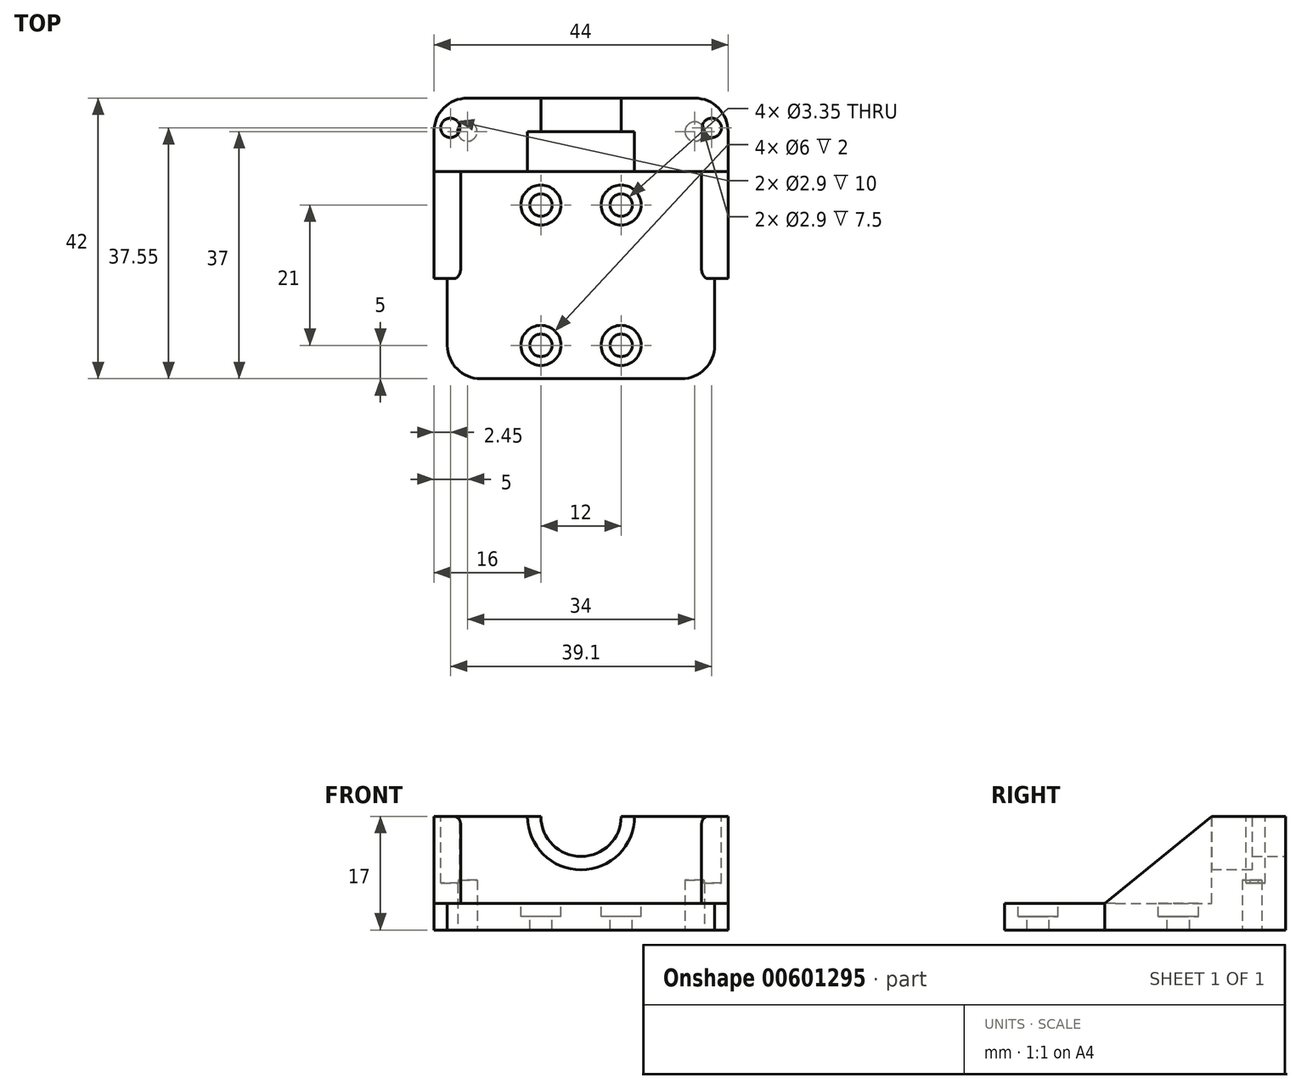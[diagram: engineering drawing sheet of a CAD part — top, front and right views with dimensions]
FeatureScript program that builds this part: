
annotation { "Feature Type Name" : "Feature", "Feature Type Description" : "" }
export const myFeature = defineFeature(function(context is Context, id is Id, definition is map)
    precondition{}
    {
        {
            var Q0;
            Q0=qCreatedBy(makeId("Top.planeOp"),FACE);
            var sketch = newSketch(context, id + "F0", { "sketchPlane" : qUnion([Q0])});
            skLineSegment(sketch, "E0.bottom", {"start": v(0, 0) * mm, "end": v(40, 0) * mm});
            skLineSegment(sketch, "E0.top", {"start": v(0, 42) * mm, "end": v(40, 42) * mm});
            skLineSegment(sketch, "E0.left", {"start": v(0, 0) * mm, "end": v(0, 42) * mm});
            skLineSegment(sketch, "E0.right", {"start": v(40, 0) * mm, "end": v(40, 42) * mm});
            skSolve(sketch);
        }
        {
            var Q0;
            Q0=qSketchRegion(id+"F0",true);
            extrude(context, id + "F1", {"entities" : qUnion([Q0]), "depth" : 4 * mm});
        }
        {
            var Q0;
            Q0=makeQuery(id+"F1.opExtrude","CAP_FACE",FACE,{"disambiguationData":[OSD([sQuery(id+"F0.wireOp",EDGE,"E0.bottom"),sQuery(id+"F0.wireOp",EDGE,"E0.top"),sQuery(id+"F0.wireOp",EDGE,"E0.left"),sQuery(id+"F0.wireOp",EDGE,"E0.right")])],"isStart":false});
            var sketch = newSketch(context, id + "F2", { "sketchPlane" : qUnion([Q0])});
            skCircle(sketch, "E1", {"center": v(14, 26) * mm, "radius": 1.68 * mm});
            skCircle(sketch, "E2", {"center": v(26, 26) * mm, "radius": 1.68 * mm});
            skCircle(sketch, "E3", {"center": v(14, 5) * mm, "radius": 1.68 * mm});
            skCircle(sketch, "E4", {"center": v(26, 5) * mm, "radius": 1.68 * mm});
            skLineSegment(sketch, "E5", {"start": v(14, 26) * mm, "end": v(0, 26) * mm});
            skLineSegment(sketch, "E6", {"start": v(26, 5) * mm, "end": v(40, 5) * mm});
            skCircle(sketch, "E7", {"center": v(14, 26) * mm, "radius": 3 * mm});
            skCircle(sketch, "E8", {"center": v(26, 26) * mm, "radius": 3 * mm});
            skCircle(sketch, "E9", {"center": v(14, 5) * mm, "radius": 3 * mm});
            skCircle(sketch, "E10", {"center": v(26, 5) * mm, "radius": 3 * mm});
            skSolve(sketch);
        }
        {
            var Q0;
            Q0=makeQuery(id+"F2.imprint","IMPRINT",FACE,{"disambiguationData":[TD([[makeQuery(id+"F2.imprint","IMPRINT",EDGE,{"derivedFrom":sQuery(id+"F2.wireOp",EDGE,"E1")}),1.0]])]});
            var Q1;
            Q1=makeQuery(id+"F2.imprint","IMPRINT",FACE,{"disambiguationData":[TD([[makeQuery(id+"F2.imprint","IMPRINT",EDGE,{"derivedFrom":sQuery(id+"F2.wireOp",EDGE,"E2")}),1.0]])]});
            var Q2;
            Q2=makeQuery(id+"F2.imprint","IMPRINT",FACE,{"disambiguationData":[TD([[makeQuery(id+"F2.imprint","IMPRINT",EDGE,{"derivedFrom":sQuery(id+"F2.wireOp",EDGE,"E4")}),1.0]])]});
            var Q3;
            Q3=makeQuery(id+"F2.imprint","IMPRINT",FACE,{"disambiguationData":[TD([[makeQuery(id+"F2.imprint","IMPRINT",EDGE,{"derivedFrom":sQuery(id+"F2.wireOp",EDGE,"E3")}),1.0]])]});
            extrude(context, id + "F3", {"entities" : qUnion([Q0, Q1, Q2, Q3]), "operationType" : NewBodyOperationType.REMOVE, "oppositeDirection" : true, "depth" : 25 * mm});
        }
        {
            var Q0;
            Q0=makeQuery(id+"F1.opExtrude","CAP_FACE",FACE,{"disambiguationData":[OSD([sQuery(id+"F0.wireOp",EDGE,"E0.bottom"),sQuery(id+"F0.wireOp",EDGE,"E0.top"),sQuery(id+"F0.wireOp",EDGE,"E0.left"),sQuery(id+"F0.wireOp",EDGE,"E0.right")])],"isStart":false});
            var sketch = newSketch(context, id + "F4", { "sketchPlane" : qUnion([Q0])});
            skLineSegment(sketch, "E11.bottom", {"start": v(0, 42) * mm, "end": v(40, 42) * mm});
            skLineSegment(sketch, "E11.top", {"start": v(0, 31) * mm, "end": v(40, 31) * mm});
            skLineSegment(sketch, "E11.left", {"start": v(0, 42) * mm, "end": v(0, 31) * mm});
            skLineSegment(sketch, "E11.right", {"start": v(40, 42) * mm, "end": v(40, 31) * mm});
            skSolve(sketch);
        }
        {
            var Q0;
            Q0=qSketchRegion(id+"F4",true);
            extrude(context, id + "F5", {"entities" : qUnion([Q0]), "operationType" : NewBodyOperationType.ADD, "depth" : 13 * mm, "offsetDistance" : 25 * mm});
        }
        {
            var Q0;
            Q0=makeQuery(id+"F5.boolean.opBoolean","MERGE",FACE,{"derivedFrom":[makeQuery(id+"F1.opExtrude","SWEPT_FACE",FACE,{"disambiguationData":[OSD([sQuery(id+"F0.wireOp",EDGE,"E0.top")])]}),makeQuery(id+"F5.opExtrude","SWEPT_FACE",FACE,{"disambiguationData":[OSD([sQuery(id+"F4.wireOp",EDGE,"E11.bottom")])]})]});
            var sketch = newSketch(context, id + "F6", { "sketchPlane" : qUnion([Q0])});
            skCircle(sketch, "E12", {"center": v(-20, 17) * mm, "radius": 6 * mm});
            skSolve(sketch);
        }
        {
            var Q0;
            {var subQ0=makeQuery(id+"F5.opExtrude","CAP_EDGE",EDGE,{"disambiguationData":[OSD([sQuery(id+"F4.wireOp",EDGE,"E11.bottom")])],"isStart":false});var subQ1=sQuery(id+"F6.wireOp",EDGE,"E12");var subQ3=makeQuery(id+"F6.imprint","INTERSECT",VERTEX,{"disambiguationData":[OD(0.0)],"derivedFrom":[subQ0,subQ1]});Q0=makeQuery(id+"F6.imprint","IMPRINT",FACE,{"disambiguationData":[TD([[makeQuery(id+"F6.imprint","IMPRINT",EDGE,{"disambiguationData":[TD([[subQ3,1.0]])],"derivedFrom":subQ1}),1.0]])]});}
            extrude(context, id + "F7", {"entities" : qUnion([Q0]), "operationType" : NewBodyOperationType.REMOVE, "oppositeDirection" : true, "depth" : 6 * mm});
        }
        {
            var Q0;
            Q0=makeQuery(id+"F5.opExtrude","SWEPT_FACE",FACE,{"disambiguationData":[OSD([sQuery(id+"F4.wireOp",EDGE,"E11.top")])]});
            var sketch = newSketch(context, id + "F8", { "sketchPlane" : qUnion([Q0])});
            skCircle(sketch, "E13", {"center": v(20, 17) * mm, "radius": 8 * mm});
            skSolve(sketch);
        }
        {
            var Q0;
            Q0=qSketchRegion(id+"F8",true);
            extrude(context, id + "F9", {"entities" : qUnion([Q0]), "operationType" : NewBodyOperationType.REMOVE, "oppositeDirection" : true, "depth" : 6 * mm});
        }
        {
            var Q0;
            Q0=makeQuery(id+"F2.imprint","IMPRINT",FACE,{"disambiguationData":[TD([[makeQuery(id+"F2.imprint","IMPRINT",EDGE,{"derivedFrom":sQuery(id+"F2.wireOp",EDGE,"E1")}),-1.0]])]});
            var Q1;
            Q1=makeQuery(id+"F2.imprint","IMPRINT",FACE,{"disambiguationData":[TD([[makeQuery(id+"F2.imprint","IMPRINT",EDGE,{"derivedFrom":sQuery(id+"F2.wireOp",EDGE,"E2")}),-1.0]])]});
            var Q2;
            Q2=makeQuery(id+"F2.imprint","IMPRINT",FACE,{"disambiguationData":[TD([[makeQuery(id+"F2.imprint","IMPRINT",EDGE,{"derivedFrom":sQuery(id+"F2.wireOp",EDGE,"E4")}),-1.0]])]});
            var Q3;
            Q3=makeQuery(id+"F2.imprint","IMPRINT",FACE,{"disambiguationData":[TD([[makeQuery(id+"F2.imprint","IMPRINT",EDGE,{"derivedFrom":sQuery(id+"F2.wireOp",EDGE,"E3")}),-1.0]])]});
            extrude(context, id + "F10", {"entities" : qUnion([Q0, Q1, Q2, Q3]), "operationType" : NewBodyOperationType.REMOVE, "oppositeDirection" : true, "depth" : 2 * mm});
        }
        {
            var Q0;
            Q0=makeQuery(id+"F5.boolean.opBoolean","MERGE",FACE,{"derivedFrom":[makeQuery(id+"F1.opExtrude","SWEPT_FACE",FACE,{"disambiguationData":[OSD([sQuery(id+"F0.wireOp",EDGE,"E0.left")])]}),makeQuery(id+"F5.opExtrude","SWEPT_FACE",FACE,{"disambiguationData":[OSD([sQuery(id+"F4.wireOp",EDGE,"E11.left")])]})]});
            var sketch = newSketch(context, id + "F11", { "sketchPlane" : qUnion([Q0])});
            skLineSegment(sketch, "E14.bottom", {"start": v(-42, 0) * mm, "end": v(-31, 0) * mm});
            skLineSegment(sketch, "E14.top", {"start": v(-42, 17) * mm, "end": v(-31, 17) * mm});
            skLineSegment(sketch, "E14.left", {"start": v(-42, 0) * mm, "end": v(-42, 17) * mm});
            skLineSegment(sketch, "E14.right", {"start": v(-31, 0) * mm, "end": v(-31, 17) * mm});
            skSolve(sketch);
        }
        {
            var Q0;
            Q0=qSketchRegion(id+"F11",true);
            extrude(context, id + "F12", {"entities" : qUnion([Q0]), "operationType" : NewBodyOperationType.ADD, "depth" : 2 * mm});
        }
        {
            var Q0;
            Q0=makeQuery(id+"F1.opExtrude","SWEPT_EDGE",EDGE,{"disambiguationData":[OSD([sQuery(id+"F0.wireOp",EDGE,"E0.bottom"),sQuery(id+"F0.wireOp",EDGE,"E0.left")])]});
            var Q1;
            Q1=makeQuery(id+"F1.opExtrude","SWEPT_EDGE",EDGE,{"disambiguationData":[OSD([sQuery(id+"F0.wireOp",EDGE,"E0.bottom"),sQuery(id+"F0.wireOp",EDGE,"E0.right")])]});
            var Q2;
            Q2=makeQuery(id+"F17.opExtrude","TWEAK_EDGE",EDGE,{"derivedFrom":[makeQuery(id+"F1.opExtrude","SWEPT_EDGE",EDGE,{"disambiguationData":[OSD([sQuery(id+"F0.wireOp",EDGE,"E0.bottom"),sQuery(id+"F0.wireOp",EDGE,"E0.left")])]}),makeQuery(id+"F12.opExtrude","CAP_FACE",FACE,{"disambiguationData":[OSD([sQuery(id+"F11.wireOp",EDGE,"E14.bottom"),sQuery(id+"F11.wireOp",EDGE,"E14.top"),sQuery(id+"F11.wireOp",EDGE,"E14.left"),sQuery(id+"F11.wireOp",EDGE,"E14.right")])],"isStart":false})]});
            fillet(context, id + "F13", {"entities" : qUnion([Q0, Q1, Q2]), "radius" : 5 * mm, "tangentPropagation" : true, "allowEdgeOverflow" : false});
        }
        {
            var Q0;
            Q0=makeQuery(id+"F5.boolean.opBoolean","MERGE",FACE,{"derivedFrom":[makeQuery(id+"F1.opExtrude","SWEPT_FACE",FACE,{"disambiguationData":[OSD([sQuery(id+"F0.wireOp",EDGE,"E0.right")])]}),makeQuery(id+"F5.opExtrude","SWEPT_FACE",FACE,{"disambiguationData":[OSD([sQuery(id+"F4.wireOp",EDGE,"E11.right")])]})]});
            var sketch = newSketch(context, id + "F14", { "sketchPlane" : qUnion([Q0])});
            skLineSegment(sketch, "E15.bottom", {"start": v(42, 0) * mm, "end": v(31, 0) * mm});
            skLineSegment(sketch, "E15.top", {"start": v(42, 17) * mm, "end": v(31, 17) * mm});
            skLineSegment(sketch, "E15.left", {"start": v(42, 0) * mm, "end": v(42, 17) * mm});
            skLineSegment(sketch, "E15.right", {"start": v(31, 0) * mm, "end": v(31, 17) * mm});
            skSolve(sketch);
        }
        {
            var Q0;
            Q0=qSketchRegion(id+"F14",true);
            extrude(context, id + "F15", {"entities" : qUnion([Q0]), "operationType" : NewBodyOperationType.ADD, "depth" : 2 * mm});
        }
        {
            var Q0;
            Q0=qSketchRegion(id+"F14",true);
            extrude(context, id + "F16", {"entities" : qUnion([Q0]), "operationType" : NewBodyOperationType.ADD, "depth" : 2 * mm});
        }
        {
            var Q0;
            Q0=makeQuery(id+"F5.boolean.opBoolean","MERGE",FACE,{"derivedFrom":[makeQuery(id+"F1.opExtrude","SWEPT_FACE",FACE,{"disambiguationData":[OSD([sQuery(id+"F0.wireOp",EDGE,"E0.left")])]}),makeQuery(id+"F5.opExtrude","SWEPT_FACE",FACE,{"disambiguationData":[OSD([sQuery(id+"F4.wireOp",EDGE,"E11.left")])]})]});
            var Q1;
            Q1=makeQuery(id+"F12.opExtrude","CAP_FACE",FACE,{"disambiguationData":[OSD([sQuery(id+"F11.wireOp",EDGE,"E14.bottom"),sQuery(id+"F11.wireOp",EDGE,"E14.top"),sQuery(id+"F11.wireOp",EDGE,"E14.left"),sQuery(id+"F11.wireOp",EDGE,"E14.right")])],"isStart":false});
            extrude(context, id + "F17", {"entities" : qUnion([Q0]), "operationType" : NewBodyOperationType.ADD, "endBound" : BoundingType.UP_TO_SURFACE, "depth" : 25 * mm, "endBoundEntityFace" : qUnion([Q1]), "offsetDistance" : 25 * mm});
        }
        {
            var Q0;
            Q0=makeQuery(id+"F5.boolean.opBoolean","MERGE",FACE,{"derivedFrom":[makeQuery(id+"F1.opExtrude","SWEPT_FACE",FACE,{"disambiguationData":[OSD([sQuery(id+"F0.wireOp",EDGE,"E0.right")])]}),makeQuery(id+"F5.opExtrude","SWEPT_FACE",FACE,{"disambiguationData":[OSD([sQuery(id+"F4.wireOp",EDGE,"E11.right")])]})]});
            var Q1;
            Q1=makeQuery(id+"F15.opExtrude","CAP_FACE",FACE,{"disambiguationData":[OSD([sQuery(id+"F14.wireOp",EDGE,"E15.bottom"),sQuery(id+"F14.wireOp",EDGE,"E15.top"),sQuery(id+"F14.wireOp",EDGE,"E15.left"),sQuery(id+"F14.wireOp",EDGE,"E15.right")])],"isStart":false});
            extrude(context, id + "F18", {"entities" : qUnion([Q0]), "operationType" : NewBodyOperationType.ADD, "endBound" : BoundingType.UP_TO_SURFACE, "depth" : 25 * mm, "endBoundEntityFace" : qUnion([Q1]), "offsetDistance" : 25 * mm});
        }
        {
            var Q0;
            {var subQ0=sQuery(id+"F4.wireOp",EDGE,"E11.bottom");var subQ1=sQuery(id+"F4.wireOp",EDGE,"E11.top");var subQ2=sQuery(id+"F4.wireOp",EDGE,"E11.left");Q0=makeQuery(id+"F9.boolean.opBoolean","SPLIT",FACE,{"disambiguationData":[TD([makeQuery(id+"F1.opExtrude","SWEPT_FACE",FACE,{"disambiguationData":[OSD([sQuery(id+"F0.wireOp",EDGE,"E0.left")])]})])],"derivedFrom":makeQuery(id+"F5.opExtrude","CAP_FACE",FACE,{"disambiguationData":[OSD([subQ0,subQ1,subQ2,sQuery(id+"F4.wireOp",EDGE,"E11.right")])],"isStart":false})});}
            var sketch = newSketch(context, id + "F19", { "sketchPlane" : qUnion([Q0])});
            skCircle(sketch, "E16", {"center": v(0.45, 37.55) * mm, "radius": 1.45 * mm});
            skCircle(sketch, "E17", {"center": v(39.55, 37.55) * mm, "radius": 1.45 * mm});
            skSolve(sketch);
        }
        {
            var Q0;
            Q0=qSketchRegion(id+"F19",true);
            extrude(context, id + "F20", {"entities" : qUnion([Q0]), "operationType" : NewBodyOperationType.REMOVE, "oppositeDirection" : true, "depth" : 10 * mm, "offsetDistance" : 25 * mm});
        }
        {
            var Q0;
            Q0=makeQuery(id+"F12.opExtrude","CAP_EDGE",EDGE,{"disambiguationData":[OSD([sQuery(id+"F11.wireOp",EDGE,"E14.left")])],"isStart":false});
            var Q1;
            Q1=makeQuery(id+"F15.opExtrude","CAP_EDGE",EDGE,{"disambiguationData":[OSD([sQuery(id+"F14.wireOp",EDGE,"E15.left")])],"isStart":false});
            fillet(context, id + "F21", {"entities" : qUnion([Q0, Q1]), "radius" : 5 * mm, "tangentPropagation" : true, "allowEdgeOverflow" : false});
        }
        {
            var Q0;
            Q0=makeQuery(id+"F2.imprint","IMPRINT",FACE,{"disambiguationData":[TD([[makeQuery(id+"F2.imprint","IMPRINT",EDGE,{"derivedFrom":sQuery(id+"F2.wireOp",EDGE,"E1")}),-1.0]])]});
            var Q1;
            Q1=makeQuery(id+"F2.imprint","IMPRINT",FACE,{"disambiguationData":[TD([[makeQuery(id+"F2.imprint","IMPRINT",EDGE,{"derivedFrom":sQuery(id+"F2.wireOp",EDGE,"E2")}),-1.0]])]});
            var Q2;
            Q2=makeQuery(id+"F2.imprint","IMPRINT",FACE,{"disambiguationData":[TD([[makeQuery(id+"F2.imprint","IMPRINT",EDGE,{"derivedFrom":sQuery(id+"F2.wireOp",EDGE,"E1")}),1.0]])]});
            var Q3;
            Q3=makeQuery(id+"F2.imprint","IMPRINT",FACE,{"disambiguationData":[TD([[makeQuery(id+"F2.imprint","IMPRINT",EDGE,{"derivedFrom":sQuery(id+"F2.wireOp",EDGE,"E2")}),1.0]])]});
            extrude(context, id + "F22", {"entities" : qUnion([Q0, Q1, Q2, Q3]), "operationType" : NewBodyOperationType.REMOVE, "depth" : 25 * mm});
        }
        {
            var Q0;
            Q0=makeQuery(id+"F15.boolean.opBoolean","MERGE",FACE,{"derivedFrom":[makeQuery(id+"F12.boolean.opBoolean","MERGE",FACE,{"derivedFrom":[makeQuery(id+"F1.opExtrude","CAP_FACE",FACE,{"disambiguationData":[OSD([sQuery(id+"F0.wireOp",EDGE,"E0.bottom"),sQuery(id+"F0.wireOp",EDGE,"E0.top"),sQuery(id+"F0.wireOp",EDGE,"E0.left"),sQuery(id+"F0.wireOp",EDGE,"E0.right")])],"isStart":true}),makeQuery(id+"F12.opExtrude","SWEPT_FACE",FACE,{"disambiguationData":[OSD([sQuery(id+"F11.wireOp",EDGE,"E14.bottom")])]})]}),makeQuery(id+"F15.opExtrude","SWEPT_FACE",FACE,{"disambiguationData":[OSD([sQuery(id+"F14.wireOp",EDGE,"E15.bottom")])]})]});
            var sketch = newSketch(context, id + "F23", { "sketchPlane" : qUnion([Q0])});
            skCircle(sketch, "E18", {"center": v(37, -37) * mm, "radius": 1.45 * mm});
            skCircle(sketch, "E19", {"center": v(3, -37) * mm, "radius": 1.45 * mm});
            skSolve(sketch);
        }
        {
            var Q0;
            Q0 = qSketchRegion(id + "F23", true);
            extrude(context, id + "F24", {"entities" : qUnion([Q0]), "operationType" : NewBodyOperationType.REMOVE, "oppositeDirection" : true, "depth" : 7.5 * mm, "offsetDistance" : 25 * mm});
        }
        {
            var Q0;
            Q0=makeQuery(id+"F17.opExtrude","SWEPT_FACE",FACE,{"disambiguationData":[OSD([sQuery(id+"F0.wireOp",EDGE,"E0.bottom"),sQuery(id+"F0.wireOp",EDGE,"E0.left"),sQuery(id+"F4.wireOp",EDGE,"E11.left")])]});
            var Q1;
            Q1=makeQuery(id+"F18.opExtrude","SWEPT_FACE",FACE,{"disambiguationData":[OSD([sQuery(id+"F0.wireOp",EDGE,"E0.bottom"),sQuery(id+"F0.wireOp",EDGE,"E0.right"),sQuery(id+"F4.wireOp",EDGE,"E11.right")])]});
            extrude(context, id + "F25", {"entities" : qUnion([Q0, Q1]), "operationType" : NewBodyOperationType.REMOVE, "oppositeDirection" : true, "depth" : 10 * mm, "offsetDistance" : 25 * mm});
        }
        {
            var Q0;
            {var subQ0=sQuery(id+"F11.wireOp",EDGE,"E14.right");var subQ1=sQuery(id+"F11.wireOp",EDGE,"E14.left");var subQ2=sQuery(id+"F11.wireOp",EDGE,"E14.top");var subQ3=sQuery(id+"F11.wireOp",EDGE,"E14.bottom");Q0=makeQuery(id+"F17.boolean.opBoolean","MERGE",FACE,{"derivedFrom":[makeQuery(id+"F12.opExtrude","CAP_FACE",FACE,{"disambiguationData":[OSD([subQ3,subQ2,subQ1,subQ0])],"isStart":false}),makeQuery(id+"F17.opExtrude","CAP_FACE",FACE,{"disambiguationData":[OSD([subQ3,subQ2,subQ1,subQ0])],"isStart":false})]});}
            var sketch = newSketch(context, id + "F26", { "sketchPlane" : qUnion([Q0])});
            skLineSegment(sketch, "E20", {"start": v(-31, 17) * mm, "end": v(-15, 4) * mm});
            skLineSegment(sketch, "E21", {"start": v(-15, 4) * mm, "end": v(-31, 4) * mm});
            skLineSegment(sketch, "E22", {"start": v(-31, 4) * mm, "end": v(-31, 17) * mm});
            skSolve(sketch);
        }
        {
            var Q0;
            Q0=makeQuery(id+"F26.imprint","IMPRINT",FACE,{"disambiguationData":[TD([[makeQuery(id+"F26.imprint","IMPRINT",EDGE,{"derivedFrom":sQuery(id+"F26.wireOp",EDGE,"E20")}),-1.0]])]});
            extrude(context, id + "F27", {"entities" : qUnion([Q0]), "operationType" : NewBodyOperationType.ADD, "oppositeDirection" : true, "depth" : 4 * mm, "offsetDistance" : 25 * mm});
        }
        {
            var Q0;
            {var subQ0=sQuery(id+"F14.wireOp",EDGE,"E15.right");var subQ1=sQuery(id+"F14.wireOp",EDGE,"E15.left");var subQ2=sQuery(id+"F14.wireOp",EDGE,"E15.top");var subQ3=sQuery(id+"F14.wireOp",EDGE,"E15.bottom");Q0=makeQuery(id+"F18.boolean.opBoolean","MERGE",FACE,{"derivedFrom":[makeQuery(id+"F15.opExtrude","CAP_FACE",FACE,{"disambiguationData":[OSD([subQ3,subQ2,subQ1,subQ0])],"isStart":false}),makeQuery(id+"F18.opExtrude","CAP_FACE",FACE,{"disambiguationData":[OSD([subQ3,subQ2,subQ1,subQ0])],"isStart":false})]});}
            var sketch = newSketch(context, id + "F28", { "sketchPlane" : qUnion([Q0])});
            skLineSegment(sketch, "E23", {"start": v(31, 17) * mm, "end": v(15, 4) * mm});
            skLineSegment(sketch, "E24", {"start": v(15, 4) * mm, "end": v(31, 4) * mm});
            skLineSegment(sketch, "E25", {"start": v(31, 4) * mm, "end": v(31, 17) * mm});
            skSolve(sketch);
        }
        {
            var Q0;
            Q0=makeQuery(id+"F28.imprint","IMPRINT",FACE,{"disambiguationData":[TD([[makeQuery(id+"F28.imprint","IMPRINT",EDGE,{"derivedFrom":sQuery(id+"F28.wireOp",EDGE,"E23")}),1.0]])]});
            extrude(context, id + "F29", {"entities" : qUnion([Q0]), "operationType" : NewBodyOperationType.ADD, "oppositeDirection" : true, "depth" : 4 * mm, "offsetDistance" : 25 * mm});
        }
        {
            var Q0;
            Q0=makeQuery(id+"F27.opExtrude","CAP_EDGE",EDGE,{"disambiguationData":[OSD([sQuery(id+"F26.wireOp",EDGE,"E21")])],"isStart":false});
            var Q1;
            Q1=makeQuery(id+"F27.opExtrude","CAP_EDGE",EDGE,{"disambiguationData":[OSD([sQuery(id+"F26.wireOp",EDGE,"E20")])],"isStart":false});
            var Q2;
            Q2=makeQuery(id+"F29.opExtrude","CAP_EDGE",EDGE,{"disambiguationData":[OSD([sQuery(id+"F28.wireOp",EDGE,"E24")])],"isStart":false});
            var Q3;
            Q3=makeQuery(id+"F29.opExtrude","CAP_EDGE",EDGE,{"disambiguationData":[OSD([sQuery(id+"F28.wireOp",EDGE,"E23")])],"isStart":false});
            fillet(context, id + "F30", {"entities" : qUnion([Q0, Q1, Q2, Q3]), "radius" : 1 * mm, "allowEdgeOverflow" : false});
        }
    });
